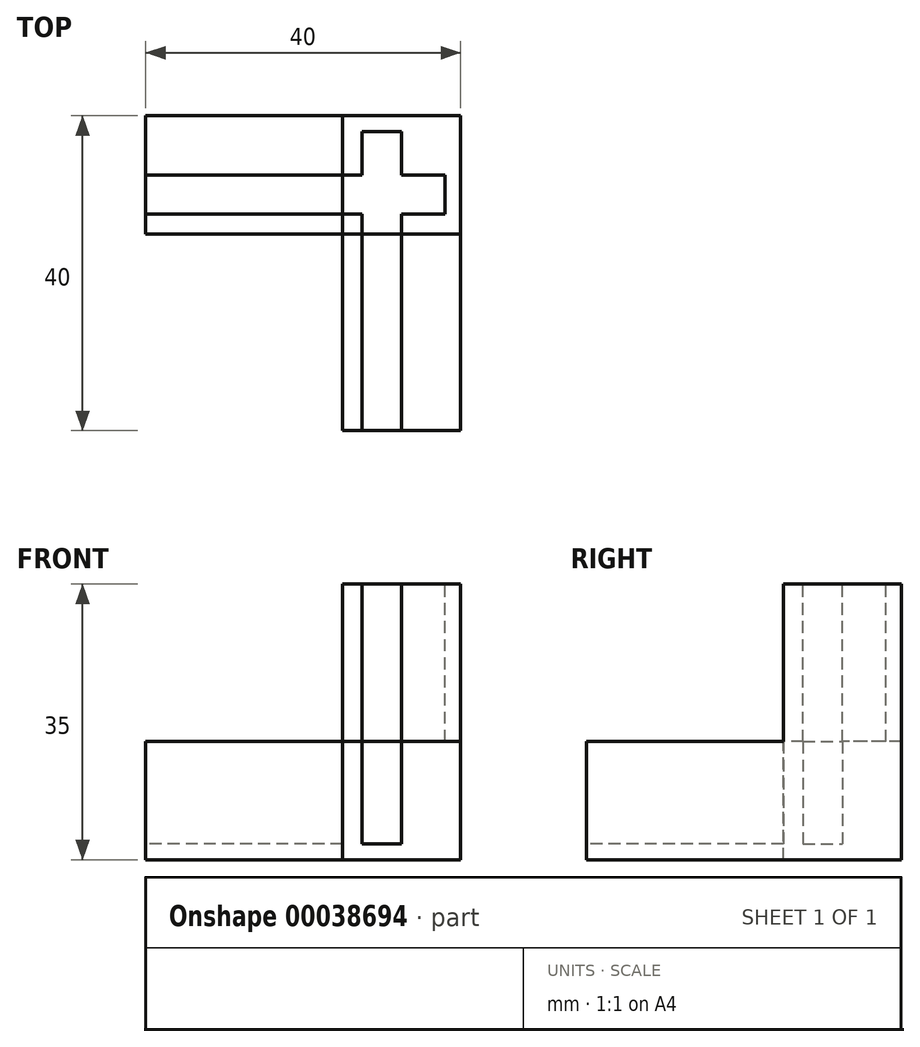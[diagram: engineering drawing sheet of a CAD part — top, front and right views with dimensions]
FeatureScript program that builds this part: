
annotation { "Feature Type Name" : "Feature", "Feature Type Description" : "" }
export const myFeature = defineFeature(function(context is Context, id is Id, definition is map)
    precondition{}
    {
        {
            var Q0;
            Q0=qCreatedBy(makeId("Top.planeOp"),FACE);
            var sketch = newSketch(context, id + "F0", { "sketchPlane" : qUnion([Q0])});
            skLineSegment(sketch, "E0.bottom", {"start": v(0, 0) * mm, "end": v(15, 0) * mm});
            skLineSegment(sketch, "E0.top", {"start": v(0, -15) * mm, "end": v(15, -15) * mm});
            skLineSegment(sketch, "E0.left", {"start": v(0, 0) * mm, "end": v(0, -15) * mm});
            skLineSegment(sketch, "E0.right", {"start": v(15, 0) * mm, "end": v(15, -15) * mm});
            skSolve(sketch);
        }
        {
            var Q0;
            Q0=makeQuery(id+"F0.imprint","IMPRINT",FACE,{"disambiguationData":[TD([[makeQuery(id+"F0.imprint","IMPRINT",EDGE,{"derivedFrom":sQuery(id+"F0.wireOp",EDGE,"E0.bottom")}),-1.0]])]});
            extrude(context, id + "F1", {"entities" : qUnion([Q0]), "depth" : 25 * mm});
        }
        {
            var Q0;
            Q0=makeQuery(id+"F1.opExtrude","SWEPT_FACE",FACE,{"disambiguationData":[OSD([sQuery(id+"F0.wireOp",EDGE,"E0.top")])]});
            var sketch = newSketch(context, id + "F2", { "sketchPlane" : qUnion([Q0])});
            skLineSegment(sketch, "E1.bottom", {"start": v(0, 0) * mm, "end": v(15, 0) * mm});
            skLineSegment(sketch, "E1.top", {"start": v(0, 15) * mm, "end": v(15, 15) * mm});
            skLineSegment(sketch, "E1.left", {"start": v(0, 0) * mm, "end": v(0, 15) * mm});
            skLineSegment(sketch, "E1.right", {"start": v(15, 0) * mm, "end": v(15, 15) * mm});
            skSolve(sketch);
        }
        {
            var Q0;
            Q0 = qSketchRegion(id + "F2", true);
            extrude(context, id + "F3", {"entities" : qUnion([Q0]), "operationType" : NewBodyOperationType.ADD, "depth" : 25 * mm});
        }
        {
            var Q0;
            Q0=makeQuery(id+"F1.opExtrude","CAP_FACE",FACE,{"disambiguationData":[OSD([sQuery(id+"F0.wireOp",EDGE,"E0.bottom"),sQuery(id+"F0.wireOp",EDGE,"E0.top"),sQuery(id+"F0.wireOp",EDGE,"E0.left"),sQuery(id+"F0.wireOp",EDGE,"E0.right")])],"isStart":false});
            extrude(context, id + "F4", {"entities" : qUnion([Q0]), "operationType" : NewBodyOperationType.ADD, "depth" : 10 * mm});
        }
        {
            var Q0;
            {var subQ0=sQuery(id+"F0.wireOp",EDGE,"E0.left");Q0=makeQuery(id+"F4.boolean.opBoolean","MERGE",FACE,{"derivedFrom":[makeQuery(id+"F3.boolean.opBoolean","MERGE",FACE,{"derivedFrom":[makeQuery(id+"F1.opExtrude","SWEPT_FACE",FACE,{"disambiguationData":[OSD([subQ0])]}),makeQuery(id+"F3.opExtrude","SWEPT_FACE",FACE,{"disambiguationData":[OSD([sQuery(id+"F2.wireOp",EDGE,"E1.left")])]})]}),makeQuery(id+"F4.opExtrude","SWEPT_FACE",FACE,{"disambiguationData":[OSD([subQ0])]})]});}
            var sketch = newSketch(context, id + "F5", { "sketchPlane" : qUnion([Q0])});
            skLineSegment(sketch, "E2.bottom", {"start": v(0, 0) * mm, "end": v(15, 0) * mm});
            skLineSegment(sketch, "E2.top", {"start": v(0, 15) * mm, "end": v(15, 15) * mm});
            skLineSegment(sketch, "E2.left", {"start": v(0, 0) * mm, "end": v(0, 15) * mm});
            skLineSegment(sketch, "E2.right", {"start": v(15, 0) * mm, "end": v(15, 15) * mm});
            skSolve(sketch);
        }
        {
            var Q0;
            Q0 = qSketchRegion(id + "F5", true);
            extrude(context, id + "F6", {"entities" : qUnion([Q0]), "operationType" : NewBodyOperationType.ADD, "depth" : 25 * mm});
        }
        {
            var Q0;
            Q0=makeQuery(id+"F6.opExtrude","CAP_FACE",FACE,{"disambiguationData":[OSD([sQuery(id+"F5.wireOp",EDGE,"E2.bottom"),sQuery(id+"F5.wireOp",EDGE,"E2.top"),sQuery(id+"F5.wireOp",EDGE,"E2.left"),sQuery(id+"F5.wireOp",EDGE,"E2.right")])],"isStart":false});
            var sketch = newSketch(context, id + "F7", { "sketchPlane" : qUnion([Q0])});
            skPoint(sketch, "E3.oppositeSnap0", {"position": v(7.5, 15) * mm});
            skLineSegment(sketch, "E3.bottom", {"start": v(12.5, 15) * mm, "end": v(7.5, 15) * mm});
            skLineSegment(sketch, "E3.top", {"start": v(12.5, 2) * mm, "end": v(7.5, 2) * mm});
            skLineSegment(sketch, "E3.left", {"start": v(12.5, 15) * mm, "end": v(12.5, 2) * mm});
            skLineSegment(sketch, "E3.right", {"start": v(7.5, 15) * mm, "end": v(7.5, 2) * mm});
            skSolve(sketch);
        }
        {
            var Q0;
            Q0 = qSketchRegion(id + "F7", true);
            var Q1;
            {var subQ0=sQuery(id+"F0.wireOp",EDGE,"E0.left");var subQ1=makeQuery(id+"F1.opExtrude","SWEPT_FACE",FACE,{"disambiguationData":[OSD([subQ0])]});var subQ2=makeQuery(id+"F3.opExtrude","SWEPT_FACE",FACE,{"disambiguationData":[OSD([sQuery(id+"F2.wireOp",EDGE,"E1.left")])]});var subQ3=makeQuery(id+"F4.opExtrude","SWEPT_FACE",FACE,{"disambiguationData":[OSD([subQ0])]});var subQ4=sQuery(id+"F0.wireOp",EDGE,"E0.bottom");Q1=makeQuery(id+"F6.boolean.opBoolean","SPLIT",FACE,{"disambiguationData":[TD([makeQuery(id+"F1.opExtrude","SWEPT_FACE",FACE,{"disambiguationData":[OSD([subQ4])]})])],"derivedFrom":makeQuery(id+"F4.boolean.opBoolean","MERGE",FACE,{"derivedFrom":[makeQuery(id+"F3.boolean.opBoolean","MERGE",FACE,{"derivedFrom":[subQ1,subQ2]}),subQ3]})});}
            extrude(context, id + "F8", {"entities" : qUnion([Q0]), "operationType" : NewBodyOperationType.REMOVE, "endBound" : BoundingType.UP_TO_SURFACE, "oppositeDirection" : true, "endBoundEntityFace" : qUnion([Q1]), "depth" : 25 * mm});
        }
        {
            var Q0;
            Q0=makeQuery(id+"F4.opExtrude","CAP_FACE",FACE,{"disambiguationData":[OSD([sQuery(id+"F0.wireOp",EDGE,"E0.bottom"),sQuery(id+"F0.wireOp",EDGE,"E0.top"),sQuery(id+"F0.wireOp",EDGE,"E0.left"),sQuery(id+"F0.wireOp",EDGE,"E0.right")])],"isStart":false});
            var sketch = newSketch(context, id + "F9", { "sketchPlane" : qUnion([Q0])});
            skPoint(sketch, "E4.0", {"position": v(0, -12.5) * mm});
            skPoint(sketch, "E5.oppositeSnap0", {"position": v(0, -7.5) * mm});
            skLineSegment(sketch, "E5.bottom", {"start": v(0, -12.5) * mm, "end": v(13, -12.5) * mm});
            skLineSegment(sketch, "E5.top", {"start": v(0, -7.5) * mm, "end": v(13, -7.5) * mm});
            skLineSegment(sketch, "E5.left", {"start": v(0, -12.5) * mm, "end": v(0, -7.5) * mm});
            skLineSegment(sketch, "E5.right", {"start": v(13, -12.5) * mm, "end": v(13, -7.5) * mm});
            skSolve(sketch);
        }
        {
            var Q0;
            Q0=makeQuery(id+"F9.imprint","IMPRINT",FACE,{"disambiguationData":[TD([[makeQuery(id+"F9.imprint","IMPRINT",EDGE,{"derivedFrom":sQuery(id+"F9.wireOp",EDGE,"E5.bottom")}),1.0]])]});
            var Q1;
            {var subQ0=sQuery(id+"F5.wireOp",EDGE,"E2.top");var subQ4=sQuery(id+"F0.wireOp",EDGE,"E0.bottom");Q1=makeQuery(id+"F8.boolean.opBoolean","SPLIT",FACE,{"disambiguationData":[TD([makeQuery(id+"F1.opExtrude","SWEPT_FACE",FACE,{"disambiguationData":[OSD([subQ4])]})])],"derivedFrom":makeQuery(id+"F6.opExtrude","SWEPT_FACE",FACE,{"disambiguationData":[OSD([subQ0])]})});}
            extrude(context, id + "F10", {"entities" : qUnion([Q0]), "operationType" : NewBodyOperationType.REMOVE, "endBound" : BoundingType.UP_TO_SURFACE, "oppositeDirection" : true, "endBoundEntityFace" : qUnion([Q1]), "depth" : 25 * mm});
        }
        {
            var Q0;
            Q0=makeQuery(id+"F3.opExtrude","CAP_FACE",FACE,{"disambiguationData":[OSD([sQuery(id+"F2.wireOp",EDGE,"E1.bottom"),sQuery(id+"F2.wireOp",EDGE,"E1.top"),sQuery(id+"F2.wireOp",EDGE,"E1.left"),sQuery(id+"F2.wireOp",EDGE,"E1.right")])],"isStart":false});
            var sketch = newSketch(context, id + "F11", { "sketchPlane" : qUnion([Q0])});
            skLineSegment(sketch, "E6.bottom", {"start": v(2.5, 15) * mm, "end": v(7.5, 15) * mm});
            skLineSegment(sketch, "E6.top", {"start": v(2.5, 2) * mm, "end": v(7.5, 2) * mm});
            skLineSegment(sketch, "E6.left", {"start": v(7.5, 15) * mm, "end": v(7.5, 2) * mm});
            skLineSegment(sketch, "E6.right", {"start": v(2.5, 15) * mm, "end": v(2.5, 2) * mm});
            skSolve(sketch);
        }
        {
            var Q0;
            Q0=makeQuery(id+"F11.imprint","IMPRINT",FACE,{"disambiguationData":[TD([[makeQuery(id+"F11.imprint","IMPRINT",EDGE,{"derivedFrom":sQuery(id+"F11.wireOp",EDGE,"E6.bottom")}),-1.0]])]});
            var Q1;
            {var subQ0=sQuery(id+"F0.wireOp",EDGE,"E0.top");Q1=makeQuery(id+"F4.boolean.opBoolean","MERGE",FACE,{"derivedFrom":[makeQuery(id+"F1.opExtrude","SWEPT_FACE",FACE,{"disambiguationData":[OSD([subQ0])]}),makeQuery(id+"F4.opExtrude","SWEPT_FACE",FACE,{"disambiguationData":[OSD([subQ0])]})]});}
            extrude(context, id + "F12", {"entities" : qUnion([Q0]), "operationType" : NewBodyOperationType.REMOVE, "endBound" : BoundingType.UP_TO_SURFACE, "oppositeDirection" : true, "endBoundEntityFace" : qUnion([Q1]), "depth" : 25 * mm});
        }
        {
            var Q0;
            Q0=makeQuery(id+"F4.opExtrude","CAP_FACE",FACE,{"disambiguationData":[OSD([sQuery(id+"F0.wireOp",EDGE,"E0.bottom"),sQuery(id+"F0.wireOp",EDGE,"E0.top"),sQuery(id+"F0.wireOp",EDGE,"E0.left"),sQuery(id+"F0.wireOp",EDGE,"E0.right")])],"isStart":false});
            var sketch = newSketch(context, id + "F13", { "sketchPlane" : qUnion([Q0])});
            skPoint(sketch, "E7.0", {"position": v(2.5, -15) * mm});
            skPoint(sketch, "E8.0", {"position": v(7.5, -15) * mm});
            skLineSegment(sketch, "E9.bottom", {"start": v(2.5, -15) * mm, "end": v(7.5, -15) * mm});
            skLineSegment(sketch, "E9.top", {"start": v(2.5, -2) * mm, "end": v(7.5, -2) * mm});
            skLineSegment(sketch, "E9.left", {"start": v(2.5, -15) * mm, "end": v(2.5, -2) * mm});
            skLineSegment(sketch, "E9.right", {"start": v(7.5, -15) * mm, "end": v(7.5, -2) * mm});
            skSolve(sketch);
        }
        {
            var Q0;
            {var subQ3=sQuery(id+"F13.wireOp",EDGE,"E9.top");Q0=makeQuery(id+"F13.imprint","IMPRINT",FACE,{"disambiguationData":[TD([[makeQuery(id+"F13.imprint","IMPRINT",EDGE,{"derivedFrom":subQ3}),-1.0]])]});}
            var Q1;
            {var subQ6=sQuery(id+"F13.wireOp",EDGE,"E9.bottom");Q1=makeQuery(id+"F13.imprint","IMPRINT",FACE,{"disambiguationData":[TD([[makeQuery(id+"F13.imprint","IMPRINT",EDGE,{"derivedFrom":subQ6}),1.0]])]});}
            var Q2;
            {var subQ0=sQuery(id+"F2.wireOp",EDGE,"E1.top");var subQ2=sQuery(id+"F0.wireOp",EDGE,"E0.right");Q2=makeQuery(id+"F12.boolean.opBoolean","SPLIT",FACE,{"disambiguationData":[TD([makeQuery(id+"F1.opExtrude","SWEPT_FACE",FACE,{"disambiguationData":[OSD([subQ2])]})])],"derivedFrom":makeQuery(id+"F3.opExtrude","SWEPT_FACE",FACE,{"disambiguationData":[OSD([subQ0])]})});}
            extrude(context, id + "F14", {"entities" : qUnion([Q0, Q1]), "operationType" : NewBodyOperationType.REMOVE, "endBound" : BoundingType.UP_TO_SURFACE, "oppositeDirection" : true, "endBoundEntityFace" : qUnion([Q2]), "depth" : 25 * mm});
        }
    });
